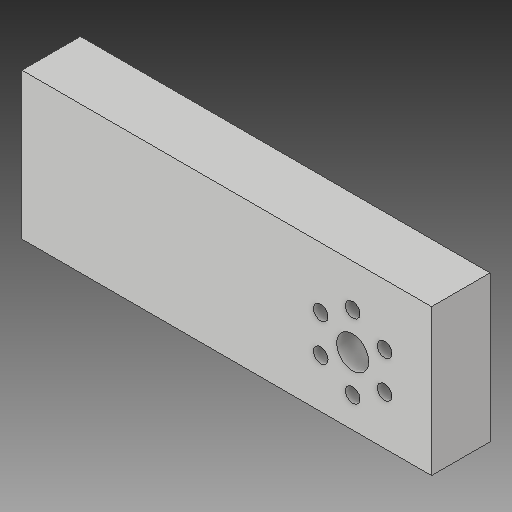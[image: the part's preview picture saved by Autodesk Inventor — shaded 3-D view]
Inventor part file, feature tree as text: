
AUTODESK INVENTOR PART (.ipt)
format: ipt  version: 2019 (Build 230136000, 136)  size: 133,120 bytes
history: native  units: in
note: dims shown in document units (in); Inventor stores cm internally (conversion verified against a paired STEP export)
features: sketch x3, extrude x2, thicken_offset x1, hole x1
ambient origin geometry x8: Origin, YZ Plane, XZ Plane, XY Plane, X Axis, Y Axis, Z Axis, Center Point
bodies: Solid1 (feature_tree)
feature tree (7):
  extrude  "Extrusion1"  Depth=1.25in
  extrude  "Extrusion2"  Depth=0.5in
  thicken_offset  "Thicken1"
  hole  "Hole1"  [1 undecoded]
  sketch  "Sketch1"  dims[d0=2.5in d1=1.25in]
  sketch  "Sketch2"  dims[d2=0.5in d3=0.0in d6=0.575in]
  sketch  "Sketch4"  dims[d7=90.0deg d8=0.275in d9=0.63in d10=0.125in d11=2.3622in d13=360.0deg d15=0.75in d16=0.0in d17=0.674in d28=1.0in d29=1.0in d35=0.13in d36=0.25in d37=0.375in d38=0.25in d39=0.5635in d40=0.3in d41=0.8108in d42=0.25in d43=3.5in d44=1.75in d45=0.25in]
note: 1 required parameter value undecoded (feature->parameter linkage not recoverable at this tier; creation-order binding heuristic only, values carry confidence <= 0.55)
